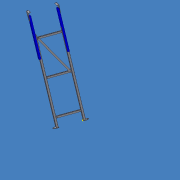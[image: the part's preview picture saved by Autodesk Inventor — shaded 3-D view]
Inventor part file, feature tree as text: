
AUTODESK INVENTOR PART (.ipt)
format: ipt  version: 2015 SP1 (Build 190203100, 203)  size: 72,704 bytes
history: native  units: mm
features: reference x2, extrude x1, sketch x1
ambient origin geometry x8: Origin, YZ Plane, XZ Plane, XY Plane, X Axis, Y Axis, Z Axis, Center Point
bodies: Solid1 (feature_tree)
feature tree (4):
  extrude  "Extrusion2"  Depth=30.0mm
  sketch  "Sketch1"  dims[d2=11.0mm d3=30.0mm d4=11.0mm d5=30.0mm d6=6.0mm d7=0.0mm]
  reference  "Reference1"
  reference  "Reference2"
